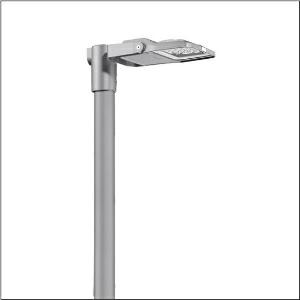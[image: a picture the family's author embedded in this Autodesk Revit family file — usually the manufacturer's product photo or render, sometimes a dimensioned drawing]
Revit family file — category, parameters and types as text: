
# Revit family: floodlight_fl_21_iq_micro___pl64_5xa7761a4e3a_8e2d
name_source: partatom
category: Lighting Fixtures
units: mm (PartAtom-declared; Revit-internal decimal feet)

## family parameters
Cut with Voids When Loaded = No
Host = Face
Light Source = No
Part Type = Normal
Room Calculation Point = No
Round Connector Dimension = Use Diameter
Shared = No

## types (1)
- --- (1 x LED, 2980 lm, 23.1 W, 4000K)
    Apparent Load = 23 VA
    CIE Flux Codes = 28 80 98 100 100
    Color Rendering = 70
    Color Temperature = 4000K
    Default Elevation = 1800 mm
    Description = Floodlight FL 21 iQ micro, floodlight, primary light control with lens, of PMMA, primary optical cover: protective disc, of toughened safety glass, transparent, light distribution: PL64, light emission: direct distribution, installation type: surface-mounted, LED, High Power LED, rated luminous flux: 2.980lm, luminous efficacy: 129lm/W, light colour: 740, colour temperature: 4000K, control: optimised constant luminous flux control (CLO 2.0), Desk-Remote (wireless, voltage-free reading and setting of iQ features in the workshop via application-optimized NFC function/RFID function), Light-Fading, Smart-Wire, Night-Set, Lumen-Switch, Temp-Guard, Auto-Match, with terminal, 6-pole, mains connection: 220..240V, AC, 50/60Hz, start of lifetime: 23W, end of service life: 24W, reduction: 11W, luminaire housing, of diecast aluminium, powder-coated, Siteco® metallic grey (DB 702S), corrosivity category C5 mid according to DIN EN ISO 12944, sealing non-destructively replaceable, please order mast flange separately, mast bracket, of steel, galvanised, powder-coated, Siteco® metallic grey (DB 702S), protection rating (complete): IP66, insulation class (complete): insulation class II (safety insulation), certification: CE, ENEC, VDE, protection symbol: D, impact resistance: IK07, permissible operating ambient temperature: -40..+40°C, permissible operating ambient temperature for outdoor applications: -40..+50°C, standard: DIN EN 12944, LABS conformity tested according to VDMA 24364:2018-05, packaging unit: 1 piece

Light Distribution: PL64
    Height = 65 mm
    Lamp = 1 x LED
    Lamp Light Flux = 2980 lm
    Lamp Power = 23.1 W
    Lamp count = 1
    Length = 312 mm
    Luminous efficacy = 129 lm/W
    Manufacturer = Siteco
    ModVariant = No
    Model = 5XA7761A4E3A
    Number of Poles = 1
    OnlyDefault = Yes
    Power Factor = 1
    Product Name = Floodlight FL 21 iQ micro | PL64
    Product group = floodlight | pylon annexe
    ProductGroupID = 6200
    Protection Class = Protection class II
    Protection Degree = IP 66
    RLX_Detail_Level = 1
    RLX_Emergency_Light_Flux = 0 lm
    RLX_Emergency_Type = 0
    RLX_Emergency_Type_DB = No
    RlxData = <blob elided: 101593 chars, md5=5b1b379b>
    Socket = socket
    Standby Power = 0 W
    System Light Flux = 2980 lm
    System Power = 23 W
    Type Comments = factory setting: luminous flux: 100 % | dim-lin: 254 | 455 mA
    Type Image = l_1007121.jpg
    URL = http://relux.com
    VarID = @adj_152259
    Voltage = 0 V
    Weight = 0.00 kg
    Width = 230 mm

## geometry (parser evidence)
native form markers: Blend x4, Sweep x12
no freeform markers — native parametric forms only
